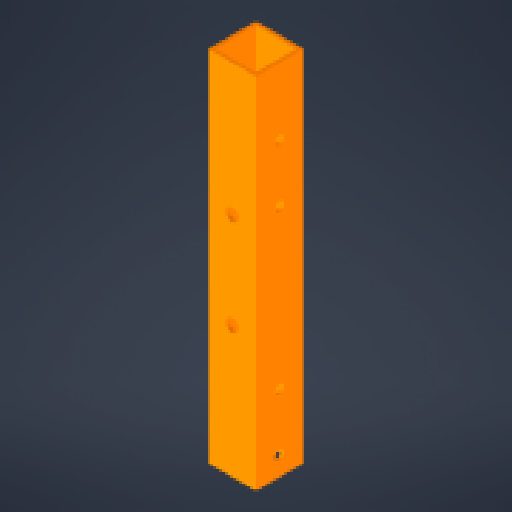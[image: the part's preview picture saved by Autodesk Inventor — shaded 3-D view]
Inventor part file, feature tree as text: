
AUTODESK INVENTOR PART (.ipt)
format: ipt  version: 2024 (Build 280153000, 153)  size: 163,840 bytes
history: native  units: mm
features: other x5, reference x4, extrude x3, sketch x3
ambient origin geometry x8: Origin, YZ Plane, XZ Plane, XY Plane, X Axis, Y Axis, Z Axis, Center Point
bodies: Body1 (feature_tree)
feature tree (15):
  other  "Твердое тело1"
  extrude  "Выдавливание1"  Depth=20.0mm
  extrude  "Выдавливание2"  Depth=1.5mm
  extrude  "Выдавливание3"  Depth=130.0mm TaperAngle=0.0deg
  sketch  "Эскиз1"
  sketch  "Эскиз2"
  sketch  "Эскиз3"
  reference  "Ссылка1"
  reference  "Ссылка2"
  reference  "Ссылка3"
  reference  "Ссылка4"
  parser-record x1  (decoder bookkeeping rows leaked as tree rows — omitted from the tree; the rows remain in map.json)
  other  "base_assambly.iam"
  other  "fb_axis:1"
  other  "fb_axis:2"
note: 1 file-system path scrubbed to <path> (originals preserved in map.json)
